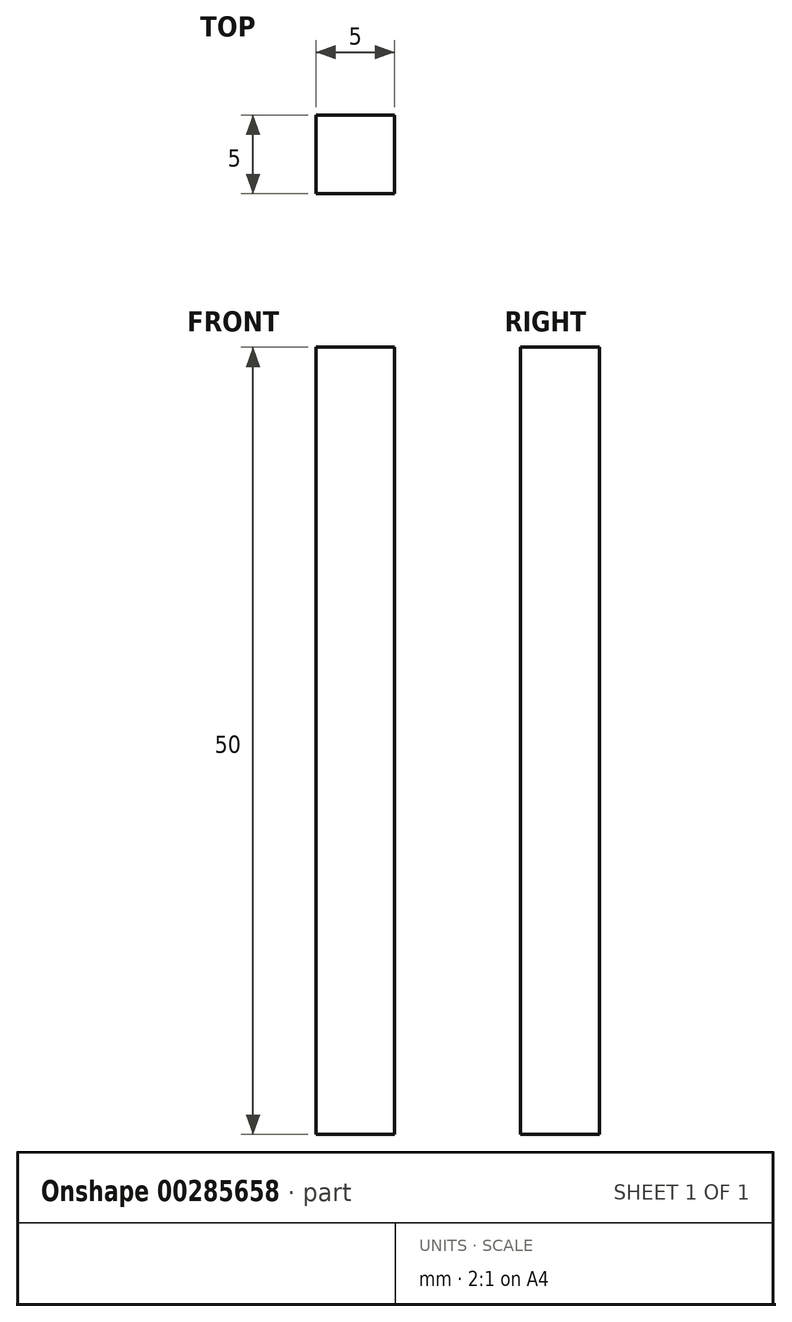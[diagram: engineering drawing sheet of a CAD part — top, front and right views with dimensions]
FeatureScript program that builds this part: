
annotation { "Feature Type Name" : "Feature", "Feature Type Description" : "" }
export const myFeature = defineFeature(function(context is Context, id is Id, definition is map)
    precondition{}
    {
        {
            var Q0;
            Q0=qCreatedBy(makeId("Front.planeOp"),FACE);
            var sketch = newSketch(context, id + "F0", { "sketchPlane" : qUnion([Q0])});
            skLineSegment(sketch, "E0.bottom", {"start": v(2.5, -25) * mm, "end": v(-2.5, -25) * mm});
            skLineSegment(sketch, "E0.top", {"start": v(2.5, 25) * mm, "end": v(-2.5, 25) * mm});
            skLineSegment(sketch, "E0.left", {"start": v(2.5, -25) * mm, "end": v(2.5, 25) * mm});
            skLineSegment(sketch, "E0.right", {"start": v(-2.5, -25) * mm, "end": v(-2.5, 25) * mm});
            skPoint(sketch, "E0.middle", {"position": v(0, 0) * mm});
            skSolve(sketch);
        }
        {
            var Q0;
            Q0 = qSketchRegion(id + "F0", true);
            extrude(context, id + "F1", {"entities" : qUnion([Q0]), "depth" : 5 * mm, "offsetDistance" : 25 * mm});
        }
    });
